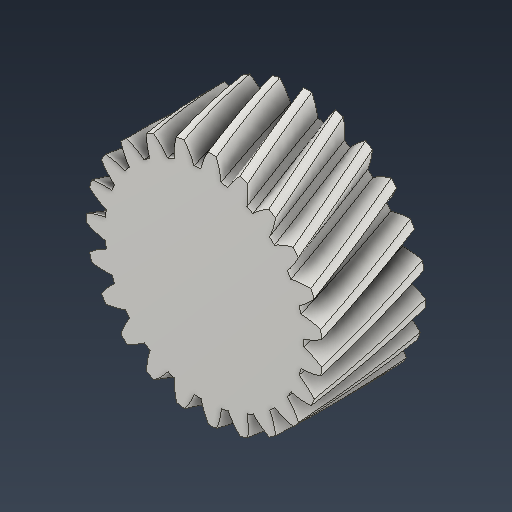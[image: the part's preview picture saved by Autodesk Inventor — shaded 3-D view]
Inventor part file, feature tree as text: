
AUTODESK INVENTOR PART (.ipt)
format: ipt  version: 2022 (Build 260153000, 153)  size: 534,016 bytes
history: native  units: mm (DEFAULTED — no unit token found)
features: plane x3, other x3, sketch x2, extrude x1
ambient origin geometry x8: Origin, YZ Plane, XZ Plane, XY Plane, X Axis, Y Axis, Z Axis, Center Point
bodies: Solid1 (feature_tree)
feature tree (9):
  extrude  "Extrusion1"  Depth=20.0mm TaperAngle=0.0deg
  plane  "Work Plane2"
  plane  "Work Plane8"
  plane  "Work Plane9"
  other  "Spur Gear"
  sketch  "Sketch1"  dims[d0=45.675945mm d1=20.0mm d2=0.0mm]
  sketch  "Sketch2"  dims[d3=42.833155mm d4=10.0mm d5=0.0mm d16=104.0mm d17=0.0mm d34=1.36591mm d39=0.0mm d41=0.0mm d43=104.0mm d46=104.0mm d47=0.0mm d48=0.0mm]
  other  "Srf1"
  other  "Pitch Diameter"
